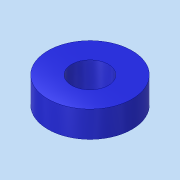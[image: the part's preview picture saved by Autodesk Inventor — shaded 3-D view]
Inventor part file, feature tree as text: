
AUTODESK INVENTOR PART (.ipt)
format: ipt  version: 2018 (Build 220112000, 112)  size: 83,456 bytes
history: native  units: mm
features: extrude x1, sketch x1
ambient origin geometry x8: Origin, YZ Plane, XZ Plane, XY Plane, X Axis, Y Axis, Z Axis, Center Point
bodies: Volumenkörper1 (feature_tree)
feature tree (2):
  extrude  "Extrusion1"  Depth=2.5mm
  sketch  "Skizze1"  dims[d0=3.5mm d1=8.0mm d2=2.5mm d3=0.0mm]
